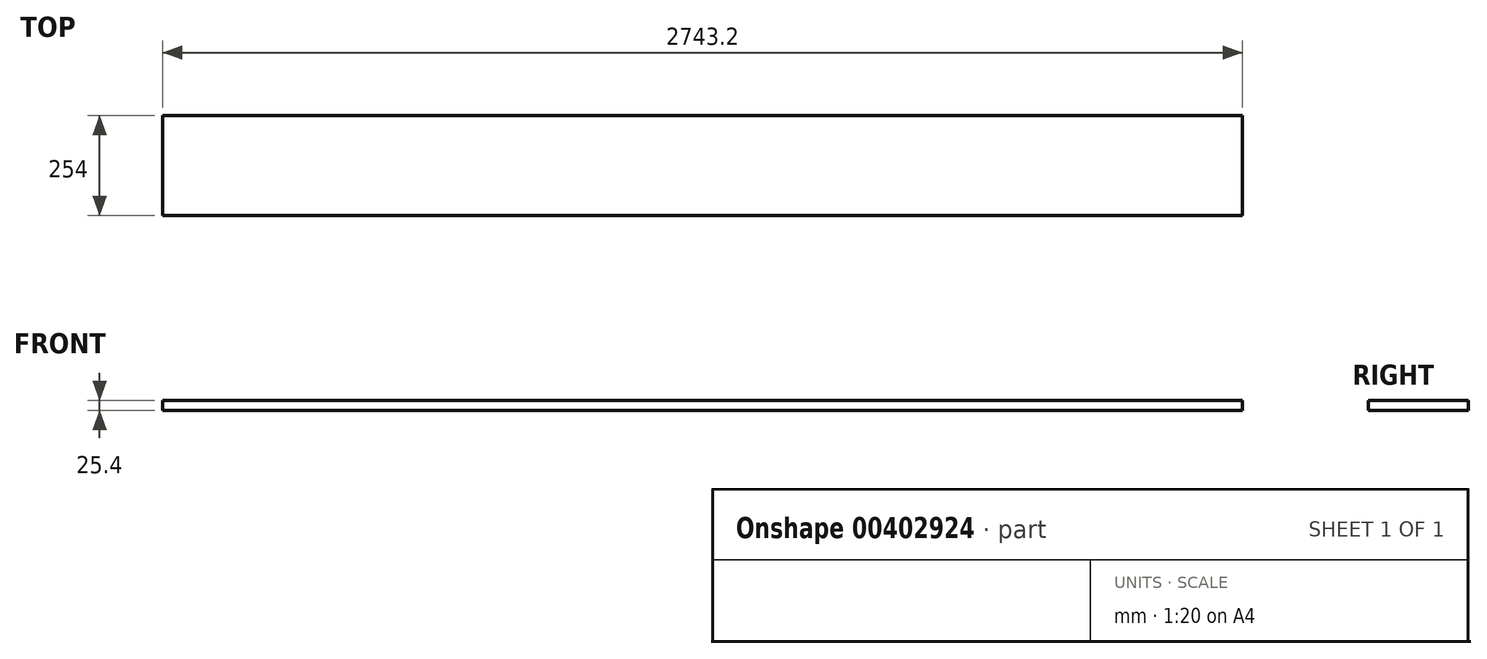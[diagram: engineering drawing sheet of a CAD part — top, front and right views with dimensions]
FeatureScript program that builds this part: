
annotation { "Feature Type Name" : "Feature", "Feature Type Description" : "" }
export const myFeature = defineFeature(function(context is Context, id is Id, definition is map)
    precondition{}
    {
        {
            var Q0;
            Q0=qCreatedBy(makeId("Top.planeOp"),FACE);
            var sketch = newSketch(context, id + "F0", { "sketchPlane" : qUnion([Q0])});
            skLineSegment(sketch, "E0.bottom", {"start": v(1371.6, -127) * mm, "end": v(-1371.6, -127) * mm});
            skLineSegment(sketch, "E0.top", {"start": v(1371.6, 127) * mm, "end": v(-1371.6, 127) * mm});
            skLineSegment(sketch, "E0.left", {"start": v(1371.6, -127) * mm, "end": v(1371.6, 127) * mm});
            skLineSegment(sketch, "E0.right", {"start": v(-1371.6, -127) * mm, "end": v(-1371.6, 127) * mm});
            skPoint(sketch, "E0.middle", {"position": v(0, 0) * mm});
            skSolve(sketch);
        }
        {
            var Q0;
            Q0 = qSketchRegion(id + "F0", true);
            extrude(context, id + "F1", {"entities" : qUnion([Q0]), "depth" : 25.4 * mm});
        }
    });
